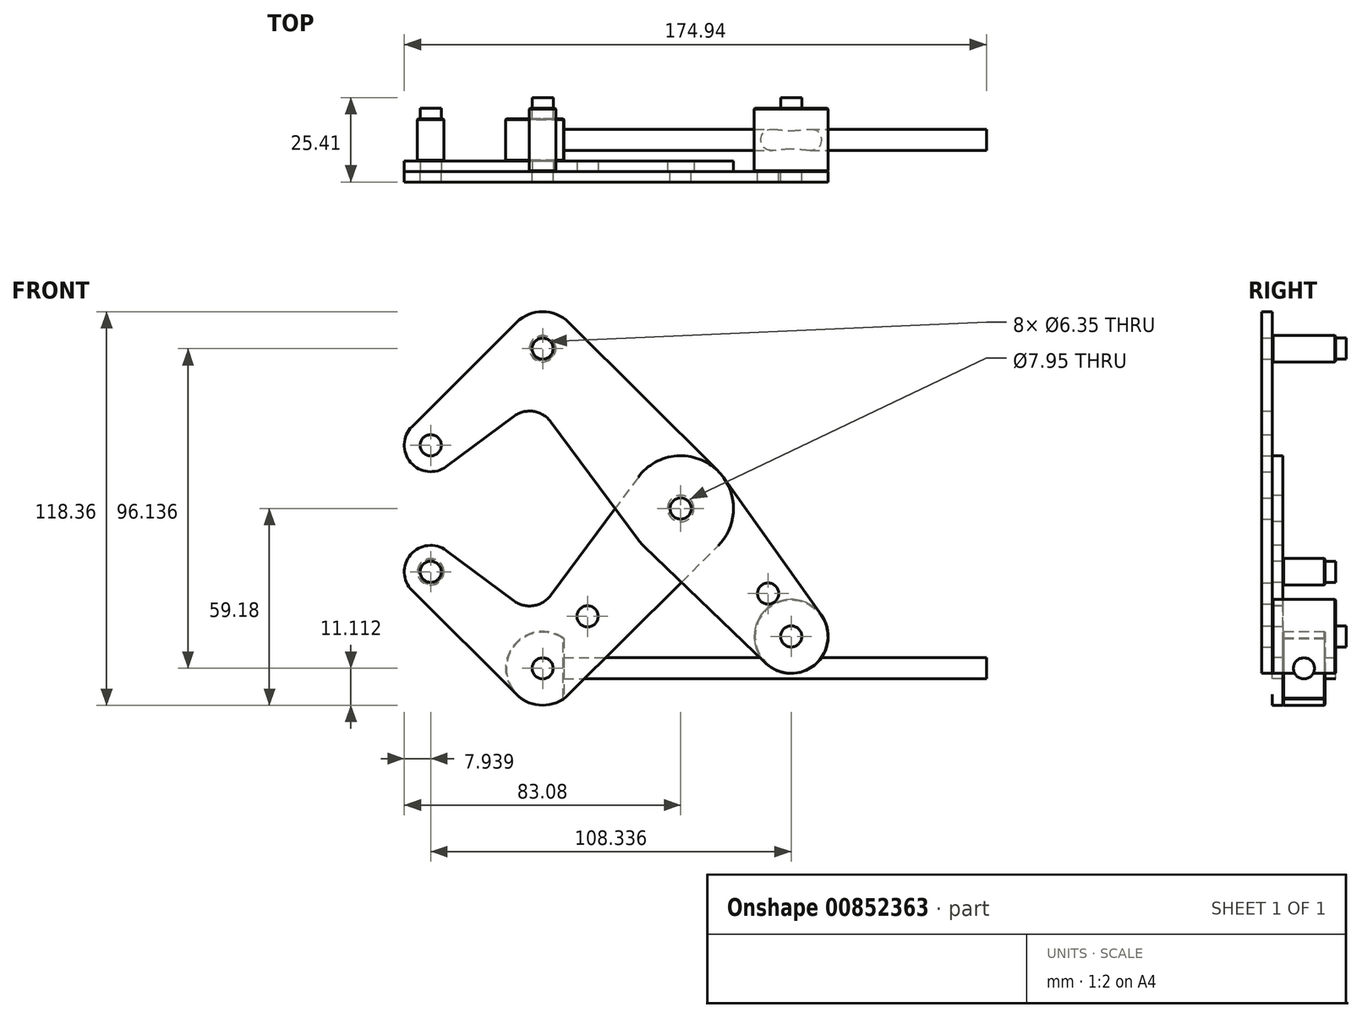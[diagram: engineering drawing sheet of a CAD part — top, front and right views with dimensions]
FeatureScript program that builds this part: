
annotation { "Feature Type Name" : "Feature", "Feature Type Description" : "" }
export const myFeature = defineFeature(function(context is Context, id is Id, definition is map)
    precondition{}
    {
        {
            var Q0;
            Q0=qCreatedBy(makeId("Front.planeOp"),FACE);
            var sketch = newSketch(context, id + "F0", { "sketchPlane" : qUnion([Q0])});
            skLineSegment(sketch, "E0", {"start": v(-41.5, 48.07) * mm, "end": v(33.2, -38.45) * mm, "construction": true});
            skLineSegment(sketch, "E1", {"start": v(-41.5, 48.07) * mm, "end": v(-75.14, 19.02) * mm, "construction": true});
            skCircle(sketch, "E2", {"center": v(0, 0) * mm, "radius": 15.88 * mm});
            skCircle(sketch, "E3", {"center": v(-41.5, 48.07) * mm, "radius": 11.11 * mm});
            skCircle(sketch, "E4", {"center": v(-75.14, 19.02) * mm, "radius": 7.94 * mm});
            skCircle(sketch, "E5", {"center": v(33.2, -38.45) * mm, "radius": 11.11 * mm});
            skCircle(sketch, "E6", {"center": v(26.27, -25.57) * mm, "radius": 3.18 * mm});
            skCircle(sketch, "E7", {"center": v(33.2, -38.45) * mm, "radius": 3.18 * mm});
            skCircle(sketch, "E8", {"center": v(-41.5, 48.07) * mm, "radius": 3.18 * mm});
            skCircle(sketch, "E9", {"center": v(-75.14, 19.02) * mm, "radius": 3.18 * mm});
            skCircle(sketch, "E10", {"center": v(0, 0) * mm, "radius": 3.98 * mm});
            skCircle(sketch, "E11", {"center": v(0, 0) * mm, "radius": 3.18 * mm});
            skPoint(sketch, "E12", {"position": v(23.87, -27.65) * mm});
            skLineSegment(sketch, "E13", {"start": v(26.27, -25.57) * mm, "end": v(23.87, -27.65) * mm, "construction": true});
            skLineSegment(sketch, "E14", {"start": v(0, 0) * mm, "end": v(-41.5, -48.07) * mm, "construction": true});
            skLineSegment(sketch, "E15", {"start": v(-41.5, -48.07) * mm, "end": v(-75.14, -19.02) * mm, "construction": true});
            skCircle(sketch, "E16", {"center": v(-41.5, -48.07) * mm, "radius": 11.11 * mm});
            skCircle(sketch, "E17", {"center": v(-75.14, -19.02) * mm, "radius": 7.94 * mm});
            skCircle(sketch, "E18", {"center": v(-75.14, -19.02) * mm, "radius": 3.18 * mm});
            skCircle(sketch, "E19", {"center": v(-41.5, -48.07) * mm, "radius": 3.18 * mm});
            skCircle(sketch, "E20", {"center": v(-28, -32.44) * mm, "radius": 3.18 * mm});
            skLineSegment(sketch, "E21", {"start": v(-80.74, 24.65) * mm, "end": v(-49.34, 55.94) * mm});
            skLineSegment(sketch, "E22", {"start": v(-33.65, 55.94) * mm, "end": v(11.2, 11.25) * mm});
            skLineSegment(sketch, "E23", {"start": v(12.94, 9.2) * mm, "end": v(42.25, -32.01) * mm});
            skLineSegment(sketch, "E24", {"start": v(25.5, -46.47) * mm, "end": v(-11, -11.45) * mm});
            skLineSegment(sketch, "E25", {"start": v(-12.76, -9.44) * mm, "end": v(-39.05, 26.08) * mm});
            skLineSegment(sketch, "E26", {"start": v(-50.19, 27.72) * mm, "end": v(-70.4, 12.66) * mm});
            skArc(sketch, "E27.filletArc", {"start": v(-39.05, 26.08) * mm, "mid": v(-44.28, 29.22) * mm, "end": v(-50.19, 27.72) * mm});
            skLineSegment(sketch, "E28", {"start": v(-75.14, 19.02) * mm, "end": v(-75.14, -19.02) * mm, "construction": true});
            skLineSegment(sketch, "E29", {"start": v(-12.76, 9.44) * mm, "end": v(-39.05, -26.08) * mm});
            skLineSegment(sketch, "E30", {"start": v(-50.19, -27.72) * mm, "end": v(-70.4, -12.66) * mm});
            skLineSegment(sketch, "E31", {"start": v(-80.74, -24.65) * mm, "end": v(-49.34, -55.94) * mm});
            skLineSegment(sketch, "E32", {"start": v(-33.65, -55.94) * mm, "end": v(11.2, -11.25) * mm});
            skArc(sketch, "E33.filletArc", {"start": v(-50.19, -27.72) * mm, "mid": v(-44.28, -29.22) * mm, "end": v(-39.05, -26.08) * mm});
            skSolve(sketch);
        }
        {
            var Q0;
            Q0=makeQuery(id+"F0.imprint","IMPRINT",FACE,{"disambiguationData":[TD([[makeQuery(id+"F0.imprint","IMPRINT",EDGE,{"derivedFrom":sQuery(id+"F0.wireOp",EDGE,"E9")}),-1.0]])]});
            var Q1;
            {var subQ0=sQuery(id+"F0.wireOp",EDGE,"E21");Q1=makeQuery(id+"F0.imprint","IMPRINT",FACE,{"disambiguationData":[TD([[makeQuery(id+"F0.imprint","IMPRINT",EDGE,{"derivedFrom":subQ0}),-1.0]])]});}
            var Q2;
            Q2=makeQuery(id+"F0.imprint","IMPRINT",FACE,{"disambiguationData":[TD([[makeQuery(id+"F0.imprint","IMPRINT",EDGE,{"derivedFrom":sQuery(id+"F0.wireOp",EDGE,"E8")}),-1.0]])]});
            var Q3;
            Q3=makeQuery(id+"F0.imprint","IMPRINT",FACE,{"disambiguationData":[TD([[makeQuery(id+"F0.imprint","IMPRINT",EDGE,{"derivedFrom":sQuery(id+"F0.wireOp",EDGE,"E10")}),-1.0]])]});
            var Q4;
            {var subQ0=sQuery(id+"F0.wireOp",EDGE,"E25");var subQ1=sQuery(id+"F0.wireOp",EDGE,"E2");var subQ2=makeQuery(id+"F0.imprint","INTERSECT",VERTEX,{"derivedFrom":[subQ1,subQ0]});Q4=makeQuery(id+"F0.imprint","IMPRINT",FACE,{"disambiguationData":[TD([[makeQuery(id+"F0.imprint","IMPRINT",EDGE,{"disambiguationData":[TD([[subQ2,1.0]])],"derivedFrom":subQ1}),-1.0]])]});}
            var Q5;
            {var subQ0=sQuery(id+"F0.wireOp",EDGE,"E24");var subQ1=sQuery(id+"F0.wireOp",EDGE,"E2");var subQ2=makeQuery(id+"F0.imprint","INTERSECT",VERTEX,{"derivedFrom":[subQ1,subQ0]});Q5=makeQuery(id+"F0.imprint","IMPRINT",FACE,{"disambiguationData":[TD([[makeQuery(id+"F0.imprint","IMPRINT",EDGE,{"disambiguationData":[TD([[subQ2,-1.0]])],"derivedFrom":subQ1}),-1.0]])]});}
            var Q6;
            Q6=makeQuery(id+"F0.imprint","IMPRINT",FACE,{"disambiguationData":[TD([[makeQuery(id+"F0.imprint","IMPRINT",EDGE,{"derivedFrom":sQuery(id+"F0.wireOp",EDGE,"E6")}),-1.0]])]});
            var Q7;
            Q7=makeQuery(id+"F0.imprint","IMPRINT",FACE,{"disambiguationData":[TD([[makeQuery(id+"F0.imprint","IMPRINT",EDGE,{"derivedFrom":sQuery(id+"F0.wireOp",EDGE,"E7")}),-1.0]])]});
            var Q8;
            Q8=makeQuery(id+"F0.imprint","IMPRINT",FACE,{"disambiguationData":[TD([[makeQuery(id+"F0.imprint","IMPRINT",EDGE,{"derivedFrom":sQuery(id+"F0.wireOp",EDGE,"E10")}),1.0]])]});
            extrude(context, id + "F1", {"entities" : qUnion([Q0, Q1, Q2, Q3, Q4, Q5, Q6, Q7, Q8]), "depth" : 3.17 * mm, "offsetDistance" : 25.4 * mm});
        }
        {
            var Q0;
            Q0=makeQuery(id+"F0.imprint","IMPRINT",FACE,{"disambiguationData":[TD([[makeQuery(id+"F0.imprint","IMPRINT",EDGE,{"derivedFrom":sQuery(id+"F0.wireOp",EDGE,"E10")}),-1.0]])]});
            var Q1;
            {var subQ0=sQuery(id+"F0.wireOp",EDGE,"E25");var subQ1=sQuery(id+"F0.wireOp",EDGE,"E2");var subQ2=makeQuery(id+"F0.imprint","INTERSECT",VERTEX,{"derivedFrom":[subQ1,subQ0]});Q1=makeQuery(id+"F0.imprint","IMPRINT",FACE,{"disambiguationData":[TD([[makeQuery(id+"F0.imprint","IMPRINT",EDGE,{"disambiguationData":[TD([[subQ2,1.0]])],"derivedFrom":subQ1}),-1.0]])]});}
            var Q2;
            {var subQ0=sQuery(id+"F0.wireOp",EDGE,"E24");var subQ1=sQuery(id+"F0.wireOp",EDGE,"E2");var subQ2=makeQuery(id+"F0.imprint","INTERSECT",VERTEX,{"derivedFrom":[subQ1,subQ0]});Q2=makeQuery(id+"F0.imprint","IMPRINT",FACE,{"disambiguationData":[TD([[makeQuery(id+"F0.imprint","IMPRINT",EDGE,{"disambiguationData":[TD([[subQ2,-1.0]])],"derivedFrom":subQ1}),-1.0]])]});}
            var Q3;
            Q3=makeQuery(id+"F0.imprint","IMPRINT",FACE,{"disambiguationData":[TD([[makeQuery(id+"F0.imprint","IMPRINT",EDGE,{"derivedFrom":sQuery(id+"F0.wireOp",EDGE,"E20")}),-1.0]])]});
            var Q4;
            Q4=makeQuery(id+"F0.imprint","IMPRINT",FACE,{"disambiguationData":[TD([[makeQuery(id+"F0.imprint","IMPRINT",EDGE,{"derivedFrom":sQuery(id+"F0.wireOp",EDGE,"E19")}),-1.0]])]});
            var Q5;
            Q5=makeQuery(id+"F0.imprint","IMPRINT",FACE,{"disambiguationData":[TD([[makeQuery(id+"F0.imprint","IMPRINT",EDGE,{"derivedFrom":sQuery(id+"F0.wireOp",EDGE,"E18")}),-1.0]])]});
            extrude(context, id + "F2", {"entities" : qUnion([Q0, Q1, Q2, Q3, Q4, Q5]), "oppositeDirection" : true, "depth" : 3.17 * mm, "offsetDistance" : 25.4 * mm});
        }
        {
            var Q0;
            Q0=makeQuery(id+"F1.opExtrude","CAP_FACE",FACE,{"disambiguationData":[OSD([sQuery(id+"F0.wireOp",EDGE,"E2"),sQuery(id+"F0.wireOp",EDGE,"E3"),sQuery(id+"F0.wireOp",EDGE,"E4"),sQuery(id+"F0.wireOp",EDGE,"E5"),sQuery(id+"F0.wireOp",EDGE,"E6"),sQuery(id+"F0.wireOp",EDGE,"E7"),sQuery(id+"F0.wireOp",EDGE,"E8"),sQuery(id+"F0.wireOp",EDGE,"E9"),sQuery(id+"F0.wireOp",EDGE,"E10"),sQuery(id+"F0.wireOp",EDGE,"E21"),sQuery(id+"F0.wireOp",EDGE,"E22"),sQuery(id+"F0.wireOp",EDGE,"E23"),sQuery(id+"F0.wireOp",EDGE,"E24"),sQuery(id+"F0.wireOp",EDGE,"E25"),sQuery(id+"F0.wireOp",EDGE,"E26"),sQuery(id+"F0.wireOp",EDGE,"E27.filletArc")])],"isStart":false});
            var sketch = newSketch(context, id + "F3", { "sketchPlane" : qUnion([Q0])});
            skCircle(sketch, "E34", {"center": v(-41.5, 48.07) * mm, "radius": 3.98 * mm});
            skCircle(sketch, "E35", {"center": v(0, 0) * mm, "radius": 3.98 * mm});
            skCircle(sketch, "E36", {"center": v(33.2, -38.45) * mm, "radius": 11.11 * mm});
            skSolve(sketch);
        }
        {
            var Q0;
            Q0=makeQuery(id+"F2.opExtrude","CAP_FACE",FACE,{"disambiguationData":[OSD([sQuery(id+"F0.wireOp",EDGE,"E2"),sQuery(id+"F0.wireOp",EDGE,"E10"),sQuery(id+"F0.wireOp",EDGE,"E16"),sQuery(id+"F0.wireOp",EDGE,"E17"),sQuery(id+"F0.wireOp",EDGE,"E18"),sQuery(id+"F0.wireOp",EDGE,"E19"),sQuery(id+"F0.wireOp",EDGE,"E20"),sQuery(id+"F0.wireOp",EDGE,"E29"),sQuery(id+"F0.wireOp",EDGE,"E30"),sQuery(id+"F0.wireOp",EDGE,"E31"),sQuery(id+"F0.wireOp",EDGE,"E32"),sQuery(id+"F0.wireOp",EDGE,"E33.filletArc")])],"isStart":true});
            var sketch = newSketch(context, id + "F4", { "sketchPlane" : qUnion([Q0])});
            skCircle(sketch, "E37", {"center": v(-41.5, -48.07) * mm, "radius": 11.11 * mm});
            skLineSegment(sketch, "E38", {"start": v(-35.14, -38.95) * mm, "end": v(-35.14, -57.19) * mm});
            skLineSegment(sketch, "E39", {"start": v(-35.14, -48.07) * mm, "end": v(33.2, -38.45) * mm, "construction": true});
            skCircle(sketch, "E40", {"center": v(-75.14, -19.02) * mm, "radius": 3.98 * mm});
            skSolve(sketch);
        }
        {
            var Q0;
            Q0=makeQuery(id+"F1.opExtrude","CAP_FACE",FACE,{"disambiguationData":[OSD([sQuery(id+"F0.wireOp",EDGE,"E2"),sQuery(id+"F0.wireOp",EDGE,"E3"),sQuery(id+"F0.wireOp",EDGE,"E4"),sQuery(id+"F0.wireOp",EDGE,"E5"),sQuery(id+"F0.wireOp",EDGE,"E6"),sQuery(id+"F0.wireOp",EDGE,"E7"),sQuery(id+"F0.wireOp",EDGE,"E8"),sQuery(id+"F0.wireOp",EDGE,"E9"),sQuery(id+"F0.wireOp",EDGE,"E11"),sQuery(id+"F0.wireOp",EDGE,"E21"),sQuery(id+"F0.wireOp",EDGE,"E22"),sQuery(id+"F0.wireOp",EDGE,"E23"),sQuery(id+"F0.wireOp",EDGE,"E24"),sQuery(id+"F0.wireOp",EDGE,"E25"),sQuery(id+"F0.wireOp",EDGE,"E26"),sQuery(id+"F0.wireOp",EDGE,"E27.filletArc")])],"isStart":true});
            cPlane(context, id + "F5", {"entities" : qUnion([Q0]), "cplaneType" : CPlaneType.OFFSET, "offset" : 9.52 * mm, "width" : 152.4 * mm, "height" : 152.4 * mm});
        }
        {
            var Q0;
            Q0=makeQuery(id+"F3.imprint","IMPRINT",FACE,{"disambiguationData":[TD([[makeQuery(id+"F3.imprint","IMPRINT",EDGE,{"derivedFrom":sQuery(id+"F3.wireOp",EDGE,"E34")}),1.0]])]});
            var Q1;
            Q1=makeQuery(id+"F3.imprint","IMPRINT",FACE,{"disambiguationData":[TD([[makeQuery(id+"F3.imprint","IMPRINT",EDGE,{"derivedFrom":makeQuery(id+"F1.opExtrude","CAP_EDGE",EDGE,{"disambiguationData":[OSD([sQuery(id+"F0.wireOp",EDGE,"E8")])],"isStart":false})}),1.0]])]});
            var Q2;
            Q2=makeQuery(id+"F3.imprint","IMPRINT",FACE,{"disambiguationData":[TD([[makeQuery(id+"F3.imprint","IMPRINT",EDGE,{"derivedFrom":makeQuery(id+"F1.opExtrude","CAP_EDGE",EDGE,{"disambiguationData":[OSD([sQuery(id+"F0.wireOp",EDGE,"E7")])],"isStart":false})}),-1.0]])]});
            var Q3;
            Q3=makeQuery(id+"F3.imprint","IMPRINT",FACE,{"disambiguationData":[TD([[makeQuery(id+"F3.imprint","IMPRINT",EDGE,{"derivedFrom":makeQuery(id+"F1.opExtrude","CAP_EDGE",EDGE,{"disambiguationData":[OSD([sQuery(id+"F0.wireOp",EDGE,"E7")])],"isStart":false})}),1.0]])]});
            var Q4;
            {var subQ2=sQuery(id+"F4.wireOp",EDGE,"E38");Q4=makeQuery(id+"F4.imprint","IMPRINT",FACE,{"disambiguationData":[TD([[makeQuery(id+"F4.imprint","IMPRINT",EDGE,{"derivedFrom":subQ2}),-1.0]])]});}
            var Q5;
            Q5=makeQuery(id+"F4.imprint","IMPRINT",FACE,{"disambiguationData":[TD([[makeQuery(id+"F4.imprint","IMPRINT",EDGE,{"derivedFrom":makeQuery(id+"F2.opExtrude","CAP_EDGE",EDGE,{"disambiguationData":[OSD([sQuery(id+"F0.wireOp",EDGE,"E19")])],"isStart":true})}),1.0]])]});
            var Q6;
            Q6=makeQuery(id+"F4.imprint","IMPRINT",FACE,{"disambiguationData":[TD([[makeQuery(id+"F4.imprint","IMPRINT",EDGE,{"derivedFrom":sQuery(id+"F4.wireOp",EDGE,"E40")}),1.0]])]});
            var Q7;
            Q7=makeQuery(id+"F4.imprint","IMPRINT",FACE,{"disambiguationData":[TD([[makeQuery(id+"F4.imprint","IMPRINT",EDGE,{"derivedFrom":makeQuery(id+"F2.opExtrude","CAP_EDGE",EDGE,{"disambiguationData":[OSD([sQuery(id+"F0.wireOp",EDGE,"E18")])],"isStart":true})}),1.0]])]});
            var Q8;
            Q8=qCreatedBy(id+"F5.planeOp",FACE);
            extrude(context, id + "F6", {"entities" : qUnion([Q0, Q1, Q2, Q3, Q4, Q5, Q6, Q7]), "endBound" : BoundingType.UP_TO_SURFACE, "oppositeDirection" : true, "depth" : 25.4 * mm, "endBoundEntityFace" : qUnion([Q8]), "offsetDistance" : 25.4 * mm});
        }
        {
            var Q0;
            Q0=makeQuery(id+"F1.opExtrude","SWEPT_BODY",BODY,{"disambiguationData":[OSD([sQuery(id+"F0.wireOp",EDGE,"E2"),sQuery(id+"F0.wireOp",EDGE,"E3"),sQuery(id+"F0.wireOp",EDGE,"E4"),sQuery(id+"F0.wireOp",EDGE,"E5"),sQuery(id+"F0.wireOp",EDGE,"E6"),sQuery(id+"F0.wireOp",EDGE,"E7"),sQuery(id+"F0.wireOp",EDGE,"E8"),sQuery(id+"F0.wireOp",EDGE,"E9"),sQuery(id+"F0.wireOp",EDGE,"E11"),sQuery(id+"F0.wireOp",EDGE,"E21"),sQuery(id+"F0.wireOp",EDGE,"E22"),sQuery(id+"F0.wireOp",EDGE,"E23"),sQuery(id+"F0.wireOp",EDGE,"E24"),sQuery(id+"F0.wireOp",EDGE,"E25"),sQuery(id+"F0.wireOp",EDGE,"E26"),sQuery(id+"F0.wireOp",EDGE,"E27.filletArc")])]});
            var Q1;
            Q1=makeQuery(id+"F2.opExtrude","SWEPT_BODY",BODY,{"disambiguationData":[OSD([sQuery(id+"F0.wireOp",EDGE,"E2"),sQuery(id+"F0.wireOp",EDGE,"E10"),sQuery(id+"F0.wireOp",EDGE,"E16"),sQuery(id+"F0.wireOp",EDGE,"E17"),sQuery(id+"F0.wireOp",EDGE,"E18"),sQuery(id+"F0.wireOp",EDGE,"E19"),sQuery(id+"F0.wireOp",EDGE,"E20"),sQuery(id+"F0.wireOp",EDGE,"E29"),sQuery(id+"F0.wireOp",EDGE,"E30"),sQuery(id+"F0.wireOp",EDGE,"E31"),sQuery(id+"F0.wireOp",EDGE,"E32"),sQuery(id+"F0.wireOp",EDGE,"E33.filletArc")])]});
            var Q2;
            Q2=makeQuery(id+"F6.opExtrude","SWEPT_BODY",BODY,{"disambiguationData":[OSD([sQuery(id+"F3.wireOp",EDGE,"E34")])]});
            var Q3;
            Q3=makeQuery(id+"F6.opExtrude","SWEPT_BODY",BODY,{"disambiguationData":[OSD([sQuery(id+"F3.wireOp",EDGE,"E36")])]});
            var Q4;
            Q4=makeQuery(id+"F6.opExtrude","SWEPT_BODY",BODY,{"disambiguationData":[OSD([sQuery(id+"F4.wireOp",EDGE,"E37"),sQuery(id+"F4.wireOp",EDGE,"E38")])]});
            var Q5;
            Q5=makeQuery(id+"F6.opExtrude","SWEPT_BODY",BODY,{"disambiguationData":[OSD([sQuery(id+"F4.wireOp",EDGE,"E40")])]});
            booleanBodies(context, id + "F7", {"operationType" : BooleanOperationType.SUBTRACTION, "tools" : qUnion([Q0, Q1]), "targets" : qUnion([Q2, Q3, Q4, Q5]), "keepTools" : true});
        }
        {
            var Q0;
            Q0=makeQuery(id+"F7.opBoolean","INTERSECT",EDGE,{"derivedFrom":[makeQuery(id+"F1.opExtrude","CAP_FACE",FACE,{"disambiguationData":[OSD([sQuery(id+"F0.wireOp",EDGE,"E2"),sQuery(id+"F0.wireOp",EDGE,"E3"),sQuery(id+"F0.wireOp",EDGE,"E4"),sQuery(id+"F0.wireOp",EDGE,"E5"),sQuery(id+"F0.wireOp",EDGE,"E6"),sQuery(id+"F0.wireOp",EDGE,"E7"),sQuery(id+"F0.wireOp",EDGE,"E8"),sQuery(id+"F0.wireOp",EDGE,"E9"),sQuery(id+"F0.wireOp",EDGE,"E11"),sQuery(id+"F0.wireOp",EDGE,"E21"),sQuery(id+"F0.wireOp",EDGE,"E22"),sQuery(id+"F0.wireOp",EDGE,"E23"),sQuery(id+"F0.wireOp",EDGE,"E24"),sQuery(id+"F0.wireOp",EDGE,"E25"),sQuery(id+"F0.wireOp",EDGE,"E26"),sQuery(id+"F0.wireOp",EDGE,"E27.filletArc")])],"isStart":true}),makeQuery(id+"F6.opExtrude","SWEPT_FACE",FACE,{"disambiguationData":[OSD([sQuery(id+"F3.wireOp",EDGE,"E34")])]})]});
            var Q1;
            Q1=makeQuery(id+"F7.opBoolean","COPY",EDGE,{"derivedFrom":makeQuery(id+"F1.opExtrude","CAP_EDGE",EDGE,{"disambiguationData":[OSD([sQuery(id+"F0.wireOp",EDGE,"E8")])],"isStart":false})});
            var Q2;
            Q2=makeQuery(id+"F7.opBoolean","COPY",EDGE,{"derivedFrom":makeQuery(id+"F2.opExtrude","CAP_EDGE",EDGE,{"disambiguationData":[OSD([sQuery(id+"F0.wireOp",EDGE,"E18")])],"isStart":true})});
            var Q3;
            Q3=makeQuery(id+"F7.opBoolean","INTERSECT",EDGE,{"derivedFrom":[makeQuery(id+"F2.opExtrude","CAP_FACE",FACE,{"disambiguationData":[OSD([sQuery(id+"F0.wireOp",EDGE,"E2"),sQuery(id+"F0.wireOp",EDGE,"E10"),sQuery(id+"F0.wireOp",EDGE,"E16"),sQuery(id+"F0.wireOp",EDGE,"E17"),sQuery(id+"F0.wireOp",EDGE,"E18"),sQuery(id+"F0.wireOp",EDGE,"E19"),sQuery(id+"F0.wireOp",EDGE,"E20"),sQuery(id+"F0.wireOp",EDGE,"E29"),sQuery(id+"F0.wireOp",EDGE,"E30"),sQuery(id+"F0.wireOp",EDGE,"E31"),sQuery(id+"F0.wireOp",EDGE,"E32"),sQuery(id+"F0.wireOp",EDGE,"E33.filletArc")])],"isStart":false}),makeQuery(id+"F6.opExtrude","SWEPT_FACE",FACE,{"disambiguationData":[OSD([sQuery(id+"F4.wireOp",EDGE,"E40")])]})]});
            var Q4;
            Q4=makeQuery(id+"F7.opBoolean","INTERSECT",EDGE,{"derivedFrom":[makeQuery(id+"F2.opExtrude","CAP_FACE",FACE,{"disambiguationData":[OSD([sQuery(id+"F0.wireOp",EDGE,"E2"),sQuery(id+"F0.wireOp",EDGE,"E10"),sQuery(id+"F0.wireOp",EDGE,"E16"),sQuery(id+"F0.wireOp",EDGE,"E17"),sQuery(id+"F0.wireOp",EDGE,"E18"),sQuery(id+"F0.wireOp",EDGE,"E19"),sQuery(id+"F0.wireOp",EDGE,"E20"),sQuery(id+"F0.wireOp",EDGE,"E29"),sQuery(id+"F0.wireOp",EDGE,"E30"),sQuery(id+"F0.wireOp",EDGE,"E31"),sQuery(id+"F0.wireOp",EDGE,"E32"),sQuery(id+"F0.wireOp",EDGE,"E33.filletArc")])],"isStart":false}),makeQuery(id+"F6.opExtrude","SWEPT_FACE",FACE,{"disambiguationData":[OSD([sQuery(id+"F4.wireOp",EDGE,"E37")])]})]});
            var Q5;
            Q5=makeQuery(id+"F7.opBoolean","COPY",EDGE,{"derivedFrom":makeQuery(id+"F2.opExtrude","CAP_EDGE",EDGE,{"disambiguationData":[OSD([sQuery(id+"F0.wireOp",EDGE,"E19")])],"isStart":true})});
            var Q6;
            Q6=makeQuery(id+"F7.opBoolean","INTERSECT",EDGE,{"derivedFrom":[makeQuery(id+"F2.opExtrude","CAP_FACE",FACE,{"disambiguationData":[OSD([sQuery(id+"F0.wireOp",EDGE,"E2"),sQuery(id+"F0.wireOp",EDGE,"E10"),sQuery(id+"F0.wireOp",EDGE,"E16"),sQuery(id+"F0.wireOp",EDGE,"E17"),sQuery(id+"F0.wireOp",EDGE,"E18"),sQuery(id+"F0.wireOp",EDGE,"E19"),sQuery(id+"F0.wireOp",EDGE,"E20"),sQuery(id+"F0.wireOp",EDGE,"E29"),sQuery(id+"F0.wireOp",EDGE,"E30"),sQuery(id+"F0.wireOp",EDGE,"E31"),sQuery(id+"F0.wireOp",EDGE,"E32"),sQuery(id+"F0.wireOp",EDGE,"E33.filletArc")])],"isStart":false}),makeQuery(id+"F6.opExtrude","SWEPT_FACE",FACE,{"disambiguationData":[OSD([sQuery(id+"F4.wireOp",EDGE,"E38")])]})]});
            var Q7;
            {var subQ0=sQuery(id+"F4.wireOp",EDGE,"E38");var subQ1=sQuery(id+"F4.wireOp",EDGE,"E37");Q7=makeQuery(id+"F6.opExtrude","SWEPT_EDGE",EDGE,{"disambiguationData":[OSD([subQ1,subQ0]),TDD([makeQuery(id+"F4.imprint","INTERSECT",VERTEX,{"disambiguationData":[OD(0.0)],"derivedFrom":[subQ1,subQ0]})])]});}
            var Q8;
            {var subQ0=sQuery(id+"F4.wireOp",EDGE,"E38");var subQ1=sQuery(id+"F4.wireOp",EDGE,"E37");Q8=makeQuery(id+"F6.opExtrude","SWEPT_EDGE",EDGE,{"disambiguationData":[OSD([subQ1,subQ0]),TDD([makeQuery(id+"F4.imprint","INTERSECT",VERTEX,{"disambiguationData":[OD(1.0)],"derivedFrom":[subQ1,subQ0]})])]});}
            var Q9;
            Q9=makeQuery(id+"F7.opBoolean","INTERSECT",EDGE,{"derivedFrom":[makeQuery(id+"F1.opExtrude","CAP_FACE",FACE,{"disambiguationData":[OSD([sQuery(id+"F0.wireOp",EDGE,"E2"),sQuery(id+"F0.wireOp",EDGE,"E3"),sQuery(id+"F0.wireOp",EDGE,"E4"),sQuery(id+"F0.wireOp",EDGE,"E5"),sQuery(id+"F0.wireOp",EDGE,"E6"),sQuery(id+"F0.wireOp",EDGE,"E7"),sQuery(id+"F0.wireOp",EDGE,"E8"),sQuery(id+"F0.wireOp",EDGE,"E9"),sQuery(id+"F0.wireOp",EDGE,"E11"),sQuery(id+"F0.wireOp",EDGE,"E21"),sQuery(id+"F0.wireOp",EDGE,"E22"),sQuery(id+"F0.wireOp",EDGE,"E23"),sQuery(id+"F0.wireOp",EDGE,"E24"),sQuery(id+"F0.wireOp",EDGE,"E25"),sQuery(id+"F0.wireOp",EDGE,"E26"),sQuery(id+"F0.wireOp",EDGE,"E27.filletArc")])],"isStart":true}),makeQuery(id+"F6.opExtrude","SWEPT_FACE",FACE,{"disambiguationData":[OSD([sQuery(id+"F3.wireOp",EDGE,"E36")])]})]});
            var Q10;
            Q10=makeQuery(id+"F7.opBoolean","COPY",EDGE,{"derivedFrom":makeQuery(id+"F1.opExtrude","CAP_EDGE",EDGE,{"disambiguationData":[OSD([sQuery(id+"F0.wireOp",EDGE,"E7")])],"isStart":false})});
            chamfer(context, id + "F8", {"entities" : qUnion([Q0, Q1, Q2, Q3, Q4, Q5, Q6, Q7, Q8, Q9, Q10]), "width" : 0.25 * mm, "tangentPropagation" : true});
        }
        {
            var Q0;
            Q0=makeQuery(id+"F6.opExtrude","SWEPT_BODY",BODY,{"disambiguationData":[OSD([sQuery(id+"F3.wireOp",EDGE,"E34")])]});
            var Q1;
            Q1=makeQuery(id+"F6.opExtrude","SWEPT_BODY",BODY,{"disambiguationData":[OSD([sQuery(id+"F4.wireOp",EDGE,"E40")])]});
            var Q2;
            Q2=makeQuery(id+"F6.opExtrude","SWEPT_BODY",BODY,{"disambiguationData":[OSD([sQuery(id+"F4.wireOp",EDGE,"E37"),sQuery(id+"F4.wireOp",EDGE,"E38")])]});
            var Q3;
            Q3=makeQuery(id+"F6.opExtrude","SWEPT_BODY",BODY,{"disambiguationData":[OSD([sQuery(id+"F3.wireOp",EDGE,"E36")])]});
            var Q4;
            Q4=qCreatedBy(id+"F5.planeOp",FACE);
            mirror(context, id + "F9", {"entities" : qUnion([Q0, Q1, Q2, Q3]), "mirrorPlane" : qUnion([Q4])});
        }
        {
            var Q0;
            Q0=makeQuery(id+"F9.opPattern","COPY",BODY,{"derivedFrom":makeQuery(id+"F6.opExtrude","SWEPT_BODY",BODY,{"disambiguationData":[OSD([sQuery(id+"F4.wireOp",EDGE,"E40")])]}),"instanceName":"1"});
            var Q1;
            Q1=makeQuery(id+"F6.opExtrude","SWEPT_BODY",BODY,{"disambiguationData":[OSD([sQuery(id+"F4.wireOp",EDGE,"E40")])]});
            var Q2;
            Q2=makeQuery(id+"F9.opPattern","COPY",BODY,{"derivedFrom":makeQuery(id+"F6.opExtrude","SWEPT_BODY",BODY,{"disambiguationData":[OSD([sQuery(id+"F3.wireOp",EDGE,"E34")])]}),"instanceName":"1"});
            var Q3;
            Q3=makeQuery(id+"F6.opExtrude","SWEPT_BODY",BODY,{"disambiguationData":[OSD([sQuery(id+"F3.wireOp",EDGE,"E34")])]});
            var Q4;
            Q4=makeQuery(id+"F9.opPattern","COPY",BODY,{"derivedFrom":makeQuery(id+"F6.opExtrude","SWEPT_BODY",BODY,{"disambiguationData":[OSD([sQuery(id+"F4.wireOp",EDGE,"E37"),sQuery(id+"F4.wireOp",EDGE,"E38")])]}),"instanceName":"1"});
            var Q5;
            Q5=makeQuery(id+"F6.opExtrude","SWEPT_BODY",BODY,{"disambiguationData":[OSD([sQuery(id+"F4.wireOp",EDGE,"E37"),sQuery(id+"F4.wireOp",EDGE,"E38")])]});
            var Q6;
            Q6=makeQuery(id+"F9.opPattern","COPY",BODY,{"derivedFrom":makeQuery(id+"F6.opExtrude","SWEPT_BODY",BODY,{"disambiguationData":[OSD([sQuery(id+"F3.wireOp",EDGE,"E36")])]}),"instanceName":"1"});
            var Q7;
            Q7=makeQuery(id+"F6.opExtrude","SWEPT_BODY",BODY,{"disambiguationData":[OSD([sQuery(id+"F3.wireOp",EDGE,"E36")])]});
            booleanBodies(context, id + "F10", {"operationType" : BooleanOperationType.UNION, "tools" : qUnion([Q0, Q1, Q2, Q3, Q4, Q5, Q6, Q7])});
        }
        {
            var Q0;
            {var subQ0=makeQuery(id+"F6.opExtrude","SWEPT_FACE",FACE,{"disambiguationData":[OSD([sQuery(id+"F4.wireOp",EDGE,"E38")])]});Q0=makeQuery(id+"F10.opBoolean","MERGE",FACE,{"derivedFrom":[subQ0,makeQuery(id+"F9.opPattern","COPY",FACE,{"derivedFrom":subQ0,"instanceName":"1"})]});}
            var sketch = newSketch(context, id + "F11", { "sketchPlane" : qUnion([Q0])});
            skLineSegment(sketch, "E41", {"start": v(3.43, -39.08) * mm, "end": v(15.62, -57.05) * mm, "construction": true});
            skLineSegment(sketch, "E42", {"start": v(15.62, -39.08) * mm, "end": v(3.43, -57.05) * mm, "construction": true});
            skCircle(sketch, "E43", {"center": v(9.53, -48.07) * mm, "radius": 3.18 * mm});
            skSolve(sketch);
        }
        {
            var Q0;
            Q0=makeQuery(id+"F11.imprint","IMPRINT",FACE,{"disambiguationData":[TD([[makeQuery(id+"F11.imprint","IMPRINT",EDGE,{"derivedFrom":sQuery(id+"F11.wireOp",EDGE,"E43")}),1.0]])]});
            extrude(context, id + "F12", {"entities" : qUnion([Q0]), "oppositeDirection" : true, "depth" : 12.7 * mm, "offsetDistance" : 25.4 * mm});
        }
        {
            var Q0;
            Q0=makeQuery(id+"F12.opExtrude","CAP_FACE",FACE,{"disambiguationData":[OSD([sQuery(id+"F11.wireOp",EDGE,"E43")])],"isStart":true});
            extrude(context, id + "F13", {"entities" : qUnion([Q0]), "operationType" : NewBodyOperationType.ADD, "depth" : 127 * mm, "offsetDistance" : 25.4 * mm});
        }
    });
